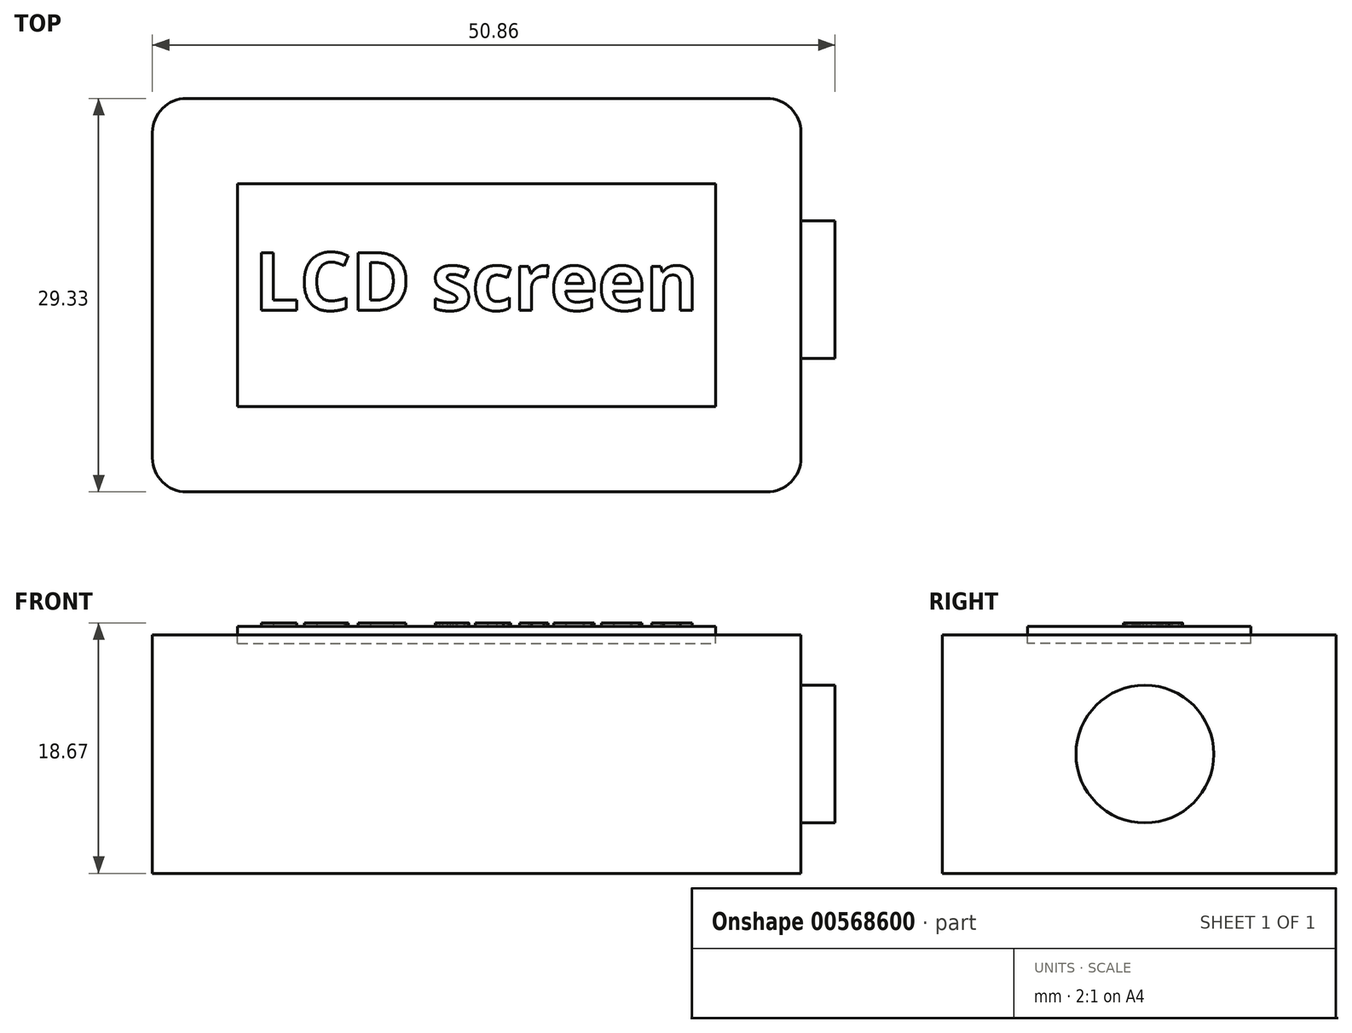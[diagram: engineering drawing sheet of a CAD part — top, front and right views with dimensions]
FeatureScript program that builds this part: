
annotation { "Feature Type Name" : "Feature", "Feature Type Description" : "" }
export const myFeature = defineFeature(function(context is Context, id is Id, definition is map)
    precondition{}
    {
        {
            var Q0;
            Q0=qCreatedBy(makeId("Top.planeOp"),FACE);
            var sketch = newSketch(context, id + "F0", { "sketchPlane" : qUnion([Q0])});
            skLineSegment(sketch, "E0.bottom", {"start": v(-21.79, 14.25) * mm, "end": v(21.45, 14.25) * mm});
            skLineSegment(sketch, "E0.top", {"start": v(-21.79, -15.08) * mm, "end": v(21.45, -15.08) * mm});
            skLineSegment(sketch, "E0.left", {"start": v(-24.33, 11.71) * mm, "end": v(-24.33, -12.54) * mm});
            skLineSegment(sketch, "E0.right", {"start": v(23.99, 11.71) * mm, "end": v(23.99, -12.54) * mm});
            skPoint(sketch, "E1.visualSharp", {"position": v(-24.33, 14.25) * mm});
            skArc(sketch, "E1.filletArc", {"start": v(-21.79, 14.25) * mm, "mid": v(-23.58, 13.5) * mm, "end": v(-24.33, 11.71) * mm});
            skPoint(sketch, "E2.visualSharp", {"position": v(-24.33, -15.08) * mm});
            skArc(sketch, "E2.filletArc", {"start": v(-24.33, -12.54) * mm, "mid": v(-23.58, -14.33) * mm, "end": v(-21.79, -15.08) * mm});
            skPoint(sketch, "E3.visualSharp", {"position": v(23.99, -15.08) * mm});
            skArc(sketch, "E3.filletArc", {"start": v(21.45, -15.08) * mm, "mid": v(23.24, -14.33) * mm, "end": v(23.99, -12.54) * mm});
            skPoint(sketch, "E4.visualSharp", {"position": v(23.99, 14.25) * mm});
            skArc(sketch, "E4.filletArc", {"start": v(23.99, 11.71) * mm, "mid": v(23.24, 13.5) * mm, "end": v(21.45, 14.25) * mm});
            skSolve(sketch);
        }
        {
            var Q0;
            Q0=makeQuery(id+"F0.imprint","IMPRINT",FACE,{"disambiguationData":[TD([[makeQuery(id+"F0.imprint","IMPRINT",EDGE,{"derivedFrom":sQuery(id+"F0.wireOp",EDGE,"E0.bottom")}),-1.0]])]});
            extrude(context, id + "F1", {"entities" : qUnion([Q0]), "oppositeDirection" : true, "depth" : 17.78 * mm, "offsetDistance" : 25.4 * mm});
        }
        {
            var Q0;
            Q0=makeQuery(id+"F1.opExtrude","CAP_FACE",FACE,{"disambiguationData":[OSD([sQuery(id+"F0.wireOp",EDGE,"E0.bottom"),sQuery(id+"F0.wireOp",EDGE,"E0.top"),sQuery(id+"F0.wireOp",EDGE,"E0.left"),sQuery(id+"F0.wireOp",EDGE,"E0.right")])],"isStart":true});
            var sketch = newSketch(context, id + "F2", { "sketchPlane" : qUnion([Q0])});
            skLineSegment(sketch, "E5.0", {"start": v(-17.98, 7.9) * mm, "end": v(17.64, 7.9) * mm});
            skLineSegment(sketch, "E5.1", {"start": v(-17.98, 7.9) * mm, "end": v(-17.98, -8.73) * mm});
            skLineSegment(sketch, "E5.2", {"start": v(-17.98, -8.73) * mm, "end": v(17.64, -8.73) * mm});
            skLineSegment(sketch, "E5.3", {"start": v(17.64, 7.9) * mm, "end": v(17.64, -8.73) * mm});
            skSolve(sketch);
        }
        {
            var Q0;
            Q0=makeQuery(id+"F2.imprint","IMPRINT",FACE,{"disambiguationData":[TD([[makeQuery(id+"F2.imprint","IMPRINT",EDGE,{"derivedFrom":sQuery(id+"F2.wireOp",EDGE,"E5.0")}),-1.0]])]});
            extrude(context, id + "F3", {"entities" : qUnion([Q0]), "endBound" : BoundingType.SYMMETRIC, "oppositeDirection" : true, "depth" : 1.27 * mm, "offsetDistance" : 25.4 * mm});
        }
        {
            var Q0;
            Q0=makeQuery(id+"F3.opExtrude","CAP_FACE",FACE,{"disambiguationData":[OSD([sQuery(id+"F2.wireOp",EDGE,"E5.0"),sQuery(id+"F2.wireOp",EDGE,"E5.1"),sQuery(id+"F2.wireOp",EDGE,"E5.2"),sQuery(id+"F2.wireOp",EDGE,"E5.3")])],"isStart":true});
            var sketch = newSketch(context, id + "F4", { "sketchPlane" : qUnion([Q0])});
            skText(sketch, "E6", { "text": "LCD screen", "fontName": "OpenSans-Bold.ttf"});
            const initialGuessF4  = {"E6": [-0.01677, -0.00154, 1, 0, 0.00433]};
            skSetInitialGuess(sketch, initialGuessF4);
            skSolve(sketch);
        }
        {
            var Q0;
            Q0 = qSketchRegion(id + "F4", true);
            extrude(context, id + "F5", {"entities" : qUnion([Q0]), "operationType" : NewBodyOperationType.ADD, "depth" : 0.25 * mm, "offsetDistance" : 25.4 * mm});
        }
        {
            var Q0;
            Q0=makeQuery(id+"F1.opExtrude","SWEPT_FACE",FACE,{"disambiguationData":[OSD([sQuery(id+"F0.wireOp",EDGE,"E0.right")])]});
            var sketch = newSketch(context, id + "F6", { "sketchPlane" : qUnion([Q0])});
            skCircle(sketch, "E7", {"center": v(0, -8.9) * mm, "radius": 5.13 * mm});
            skPoint(sketch, "E7.centerSnap0", {"position": v(-15.08, -8.9) * mm});
            skSolve(sketch);
        }
        {
            var Q0;
            Q0=makeQuery(id+"F6.imprint","IMPRINT",FACE,{"disambiguationData":[TD([[makeQuery(id+"F6.imprint","IMPRINT",EDGE,{"derivedFrom":sQuery(id+"F6.wireOp",EDGE,"E7")}),1.0]])]});
            extrude(context, id + "F7", {"entities" : qUnion([Q0]), "depth" : 2.54 * mm, "offsetDistance" : 25.4 * mm});
        }
    });
